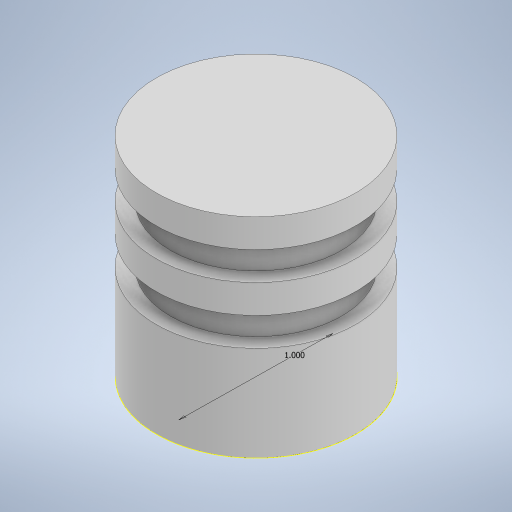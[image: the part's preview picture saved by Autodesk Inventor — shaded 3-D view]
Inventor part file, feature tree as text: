
AUTODESK INVENTOR PART (.ipt)
format: ipt  version: 2023 (Build 270158000, 158)  size: 269,312 bytes
history: native  units: in
note: dims shown in document units (in); Inventor stores cm internally (conversion verified against a paired STEP export)
features: sketch x2, revolve x1
ambient origin geometry x8: Origin, YZ Plane, XZ Plane, XY Plane, X Axis, Y Axis, Z Axis, Center Point
bodies: Body1 (feature_tree)
feature tree (3):
  revolve  "Revolution1"  [1 undecoded]
  sketch  "Sketch6"  dims[d14=0.6562in d15=0.0938in d16=0.1875in d17=0.1875in d18=0.1875in d19=0.1875in d20=90.0deg d23=1.0in]
  sketch  "Sketch5"  dims[d11=0.75in d12=0.625in]
note: 1 required parameter value undecoded (feature->parameter linkage not recoverable at this tier; creation-order binding heuristic only, values carry confidence <= 0.55)
